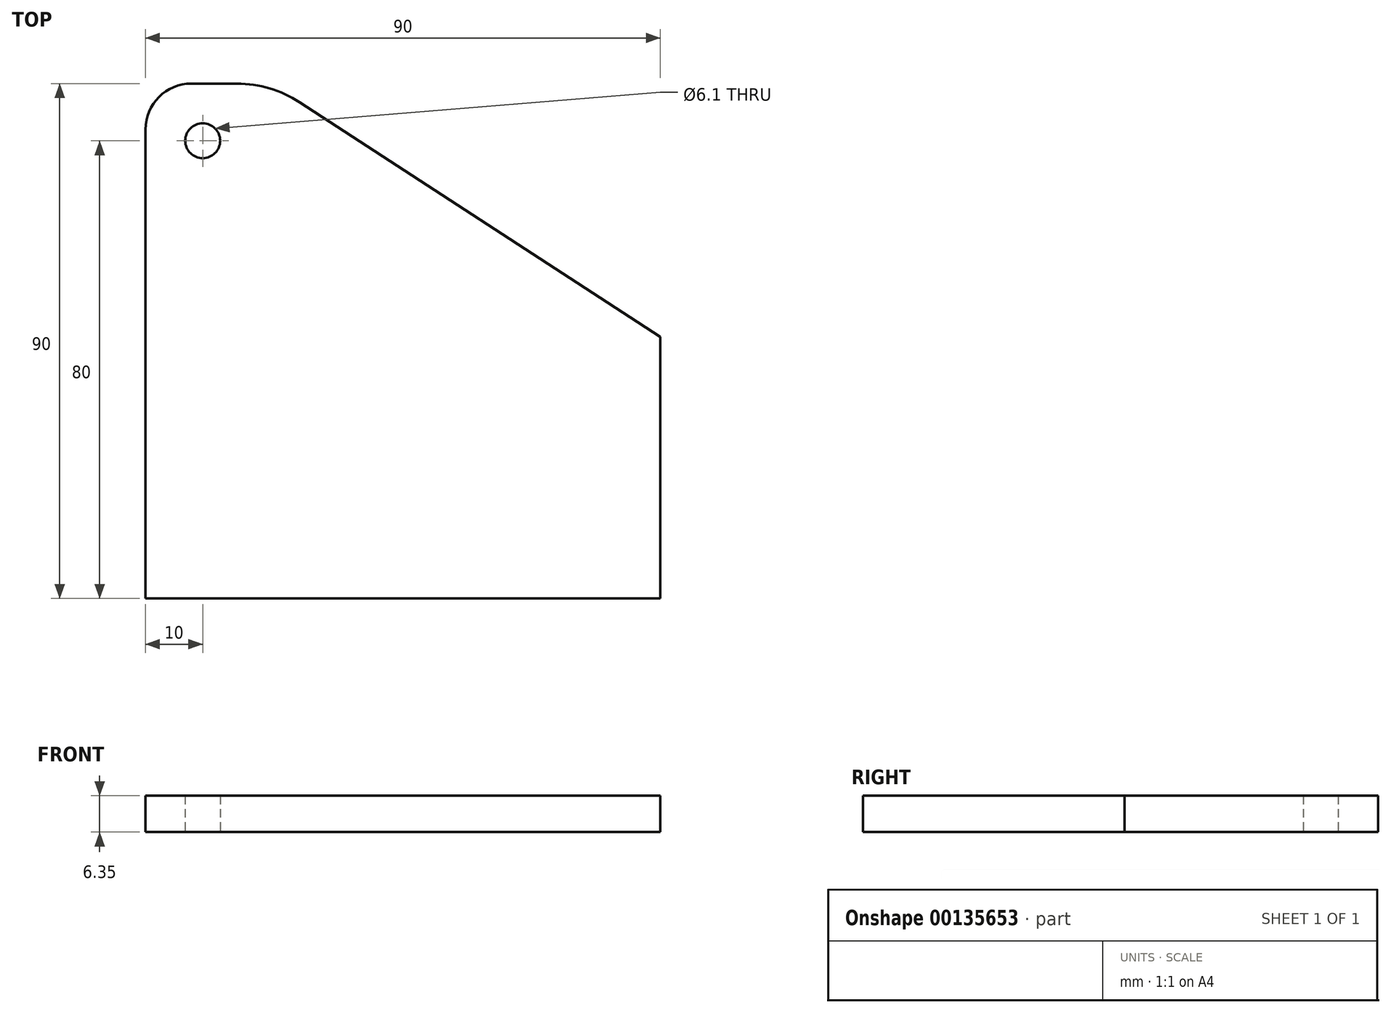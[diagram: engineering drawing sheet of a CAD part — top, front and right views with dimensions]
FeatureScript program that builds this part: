
annotation { "Feature Type Name" : "Feature", "Feature Type Description" : "" }
export const myFeature = defineFeature(function(context is Context, id is Id, definition is map)
    precondition{}
    {
        {
            var Q0;
            Q0=qCreatedBy(makeId("Top.planeOp"),FACE);
            var sketch = newSketch(context, id + "F0", { "sketchPlane" : qUnion([Q0])});
            skLineSegment(sketch, "E0.bottom", {"start": v(-45, -45) * mm, "end": v(45, -45) * mm});
            skPoint(sketch, "E0.middle", {"position": v(0, 0) * mm});
            skCircle(sketch, "E1", {"center": v(-35, 35) * mm, "radius": 3.05 * mm});
            skPoint(sketch, "E2.visualSharp", {"position": v(-45, 45) * mm});
            skPoint(sketch, "E0.right.end.orphan", {"position": v(45, 45) * mm});
            skLineSegment(sketch, "E3", {"start": v(45, -45) * mm, "end": v(45, 0.72) * mm});
            skLineSegment(sketch, "E4", {"start": v(-45, 37) * mm, "end": v(-45, -45) * mm});
            skLineSegment(sketch, "E5", {"start": v(-37, 45) * mm, "end": v(-29, 45) * mm});
            skLineSegment(sketch, "E6", {"start": v(-18.1, 41.76) * mm, "end": v(45, 0.72) * mm});
            skArc(sketch, "E7.filletArc", {"start": v(-37, 45) * mm, "mid": v(-42.66, 42.66) * mm, "end": v(-45, 37) * mm});
            skPoint(sketch, "E8.visualSharp", {"position": v(-23.07, 45) * mm});
            skArc(sketch, "E8.filletArc", {"start": v(-18.1, 41.76) * mm, "mid": v(-23.31, 44.17) * mm, "end": v(-29, 45) * mm});
            skSolve(sketch);
        }
        {
            var Q0;
            Q0=makeQuery(id+"F0.imprint","IMPRINT",FACE,{"disambiguationData":[TD([[makeQuery(id+"F0.imprint","IMPRINT",EDGE,{"derivedFrom":sQuery(id+"F0.wireOp",EDGE,"E0.bottom")}),1.0]])]});
            extrude(context, id + "F1", {"entities" : qUnion([Q0]), "depth" : 6.35 * mm});
        }
    });
